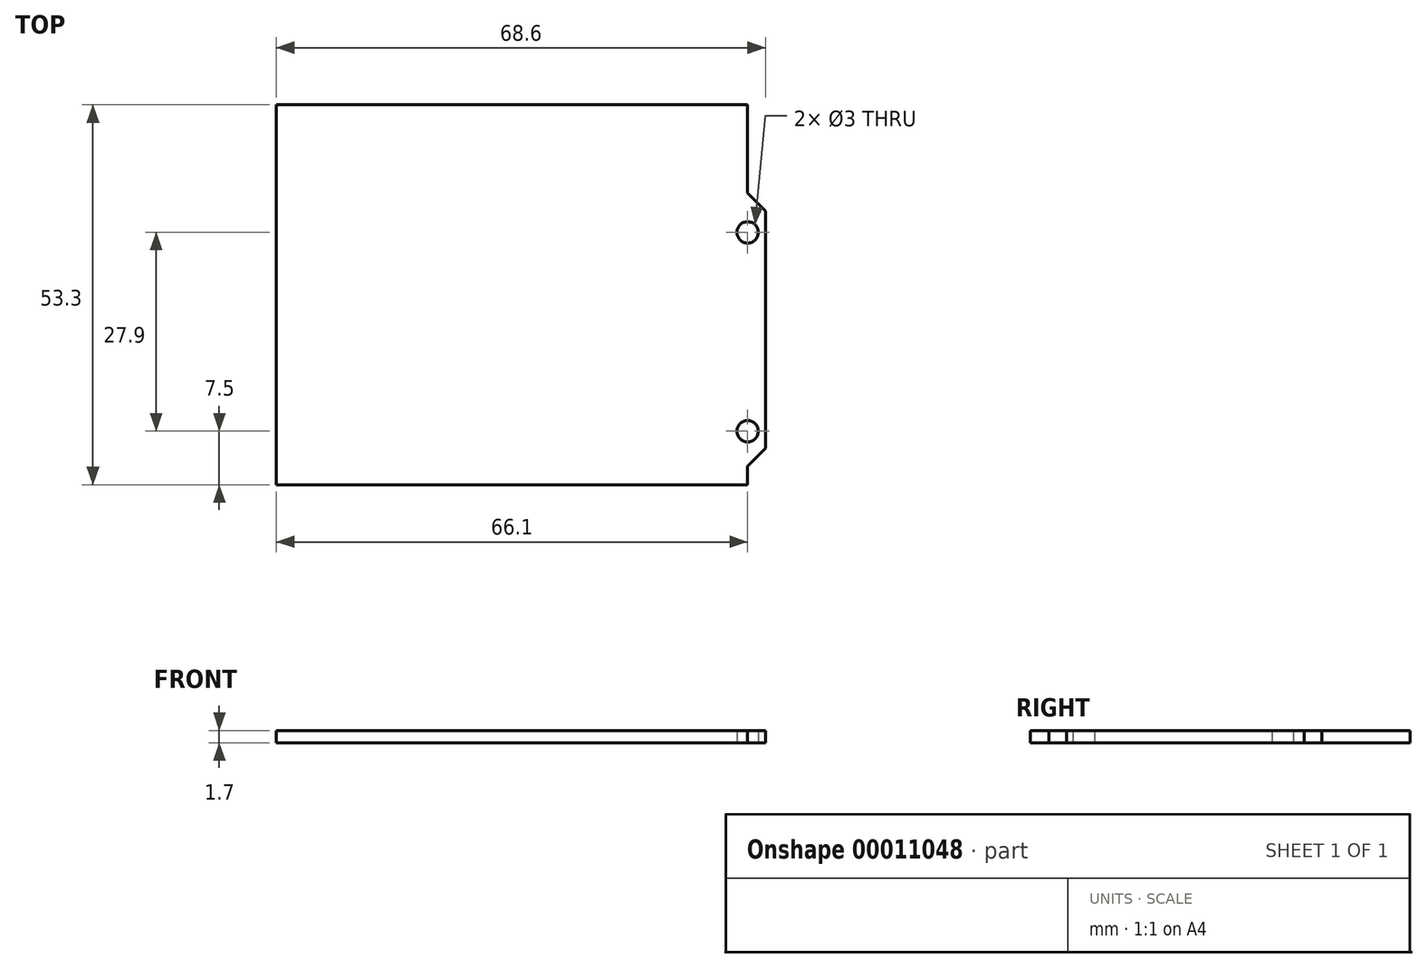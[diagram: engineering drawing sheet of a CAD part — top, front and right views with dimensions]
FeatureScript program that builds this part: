
annotation { "Feature Type Name" : "Feature", "Feature Type Description" : "" }
export const myFeature = defineFeature(function(context is Context, id is Id, definition is map)
    precondition{}
    {
        {
            var Q0;
            Q0=qCreatedBy(makeId("Top.planeOp"),FACE);
            var sketch = newSketch(context, id + "F0", { "sketchPlane" : qUnion([Q0])});
            skLineSegment(sketch, "E0", {"start": v(-34.3, 26.65) * mm, "end": v(31.8, 26.65) * mm});
            skLineSegment(sketch, "E1", {"start": v(31.8, 26.65) * mm, "end": v(31.8, 14.25) * mm});
            skLineSegment(sketch, "E2", {"start": v(31.8, 14.25) * mm, "end": v(34.3, 11.75) * mm});
            skLineSegment(sketch, "E3", {"start": v(34.3, 11.75) * mm, "end": v(34.3, -21.55) * mm});
            skLineSegment(sketch, "E4", {"start": v(34.3, -21.55) * mm, "end": v(31.8, -24.05) * mm});
            skLineSegment(sketch, "E5", {"start": v(31.8, -24.05) * mm, "end": v(31.8, -26.65) * mm});
            skLineSegment(sketch, "E6", {"start": v(31.8, -26.65) * mm, "end": v(-34.3, -26.65) * mm});
            skLineSegment(sketch, "E7", {"start": v(-34.3, -26.65) * mm, "end": v(-34.3, 26.65) * mm});
            skLineSegment(sketch, "E8", {"start": v(31.8, -26.65) * mm, "end": v(34.3, -26.65) * mm, "construction": true});
            skLineSegment(sketch, "E9", {"start": v(34.3, -26.65) * mm, "end": v(34.3, -21.55) * mm, "construction": true});
            skLineSegment(sketch, "E10", {"start": v(34.3, 11.75) * mm, "end": v(34.3, 26.65) * mm, "construction": true});
            skLineSegment(sketch, "E11", {"start": v(34.3, 26.65) * mm, "end": v(31.8, 26.65) * mm, "construction": true});
            skLineSegment(sketch, "E12", {"start": v(-34.3, 26.65) * mm, "end": v(34.3, -26.65) * mm, "construction": true});
            skLineSegment(sketch, "E13", {"start": v(34.3, 26.65) * mm, "end": v(-34.3, -26.65) * mm, "construction": true});
            skPoint(sketch, "E14", {"position": v(0, 0) * mm});
            skLineSegment(sketch, "E15", {"start": v(31.8, -24.05) * mm, "end": v(31.8, 14.25) * mm, "construction": true});
            skCircle(sketch, "E16", {"center": v(31.8, -19.15) * mm, "radius": 1.5 * mm});
            skCircle(sketch, "E17", {"center": v(31.8, 8.75) * mm, "radius": 1.5 * mm});
            skSolve(sketch);
        }
        {
            var Q0;
            Q0=makeQuery(id+"F0.imprint","IMPRINT",FACE,{"disambiguationData":[TD([[makeQuery(id+"F0.imprint","IMPRINT",EDGE,{"derivedFrom":sQuery(id+"F0.wireOp",EDGE,"E0")}),-1.0]])]});
            extrude(context, id + "F1", {"entities" : qUnion([Q0]), "depth" : 1.7 * mm});
        }
    });
